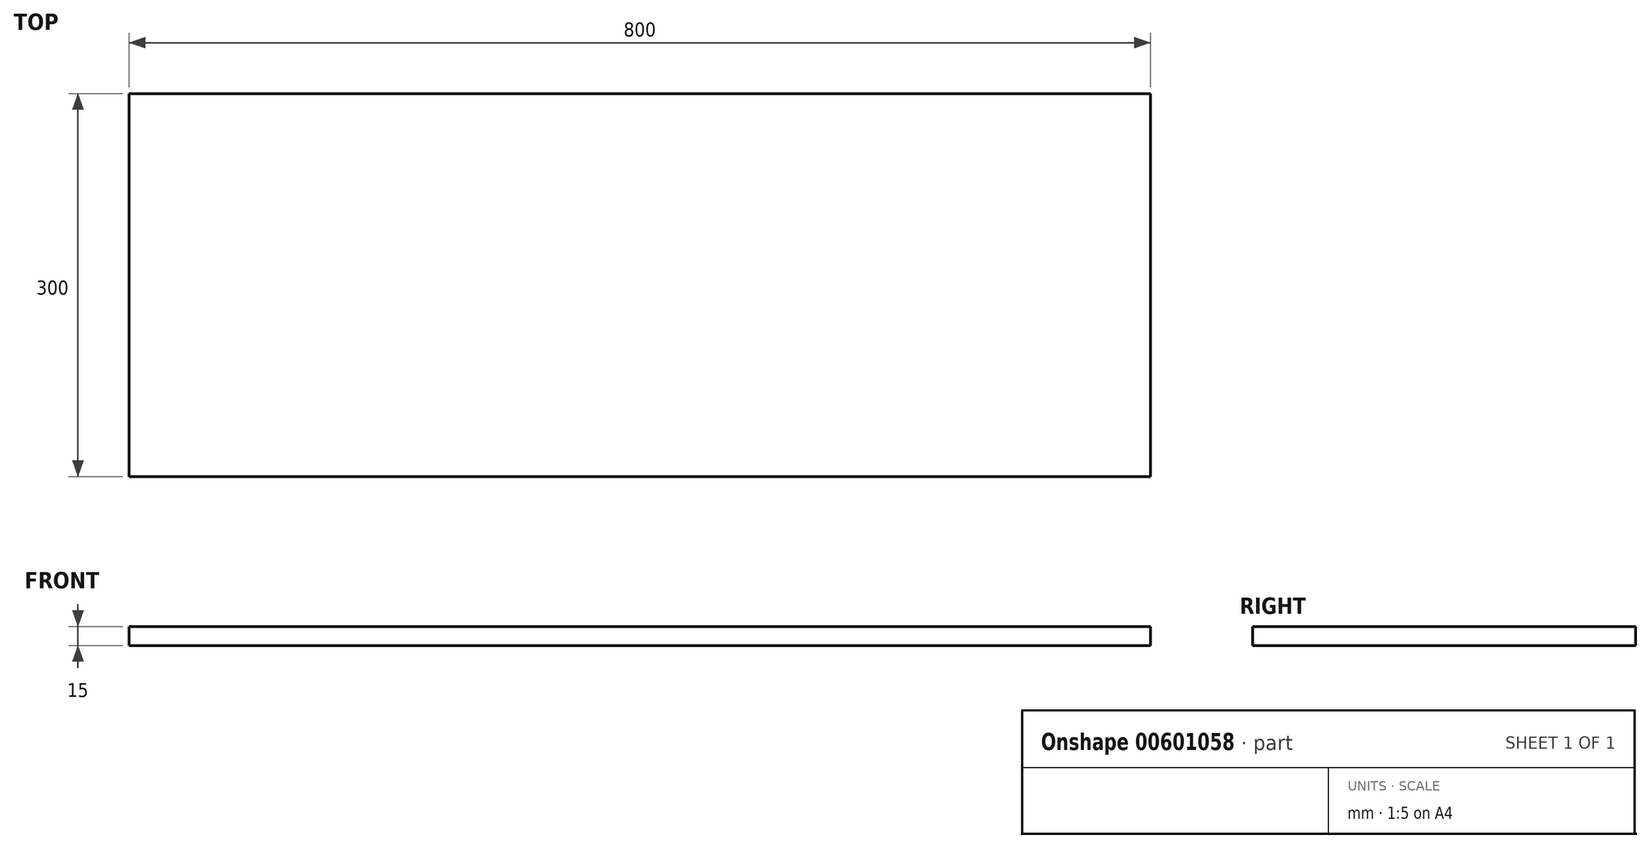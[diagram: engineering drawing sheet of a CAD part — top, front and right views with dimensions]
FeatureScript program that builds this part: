
annotation { "Feature Type Name" : "Feature", "Feature Type Description" : "" }
export const myFeature = defineFeature(function(context is Context, id is Id, definition is map)
    precondition{}
    {
        {
            var Q0;
            Q0=qCreatedBy(makeId("Top.planeOp"),FACE);
            var sketch = newSketch(context, id + "F0", { "sketchPlane" : qUnion([Q0])});
            skLineSegment(sketch, "E0.bottom", {"start": v(0, 0) * mm, "end": v(800, 0) * mm});
            skLineSegment(sketch, "E0.top", {"start": v(0, 300) * mm, "end": v(800, 300) * mm});
            skLineSegment(sketch, "E0.left", {"start": v(0, 0) * mm, "end": v(0, 300) * mm});
            skLineSegment(sketch, "E0.right", {"start": v(800, 0) * mm, "end": v(800, 300) * mm});
            skSolve(sketch);
        }
        {
            var Q0;
            Q0=makeQuery(id+"F0.imprint","IMPRINT",FACE,{"disambiguationData":[TD([[makeQuery(id+"F0.imprint","IMPRINT",EDGE,{"derivedFrom":sQuery(id+"F0.wireOp",EDGE,"E0.bottom")}),1.0]])]});
            extrude(context, id + "F1", {"entities" : qUnion([Q0]), "depth" : 15 * mm, "offsetDistance" : 25 * mm});
        }
    });
